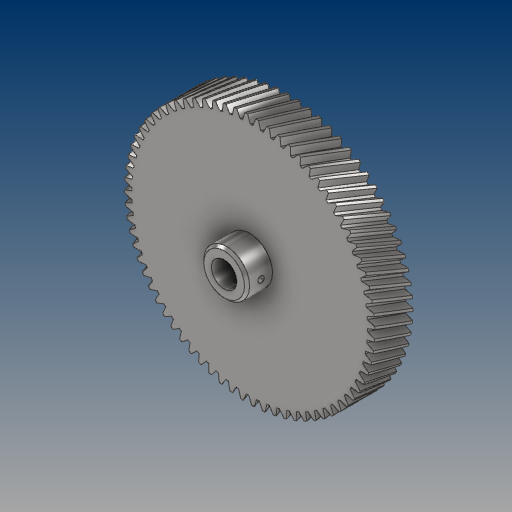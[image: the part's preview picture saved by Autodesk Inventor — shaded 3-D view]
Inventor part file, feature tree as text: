
AUTODESK INVENTOR PART (.ipt)
format: ipt  version: 2021 (Build 250183000, 183)  size: 1,323,008 bytes
history: native  units: mm (DEFAULTED — no unit token found)
features: extrude x4, sketch x4, plane x3, other x3, projected_geometry x2, chamfer x1, pattern_circular x1
ambient origin geometry x8: Origin, YZ Plane, XZ Plane, XY Plane, X Axis, Y Axis, Z Axis, Center Point
bodies: Solid1 (feature_tree)
feature tree (18):
  extrude  "Extrusion1"  Depth=15.0mm TaperAngle=0.0deg
  plane  "Work Plane2"
  plane  "Work Plane8"
  plane  "Work Plane9"
  other  "Spur Gear"
  sketch  "Sketch3"  dims[d16=59.86mm d17=0.0mm d34=0.436332mm]
  extrude  "Extrusion2"  Depth=10.0mm TaperAngle=0.0deg
  extrude  "Extrusion3"  Depth=0.436332mm TaperAngle=0.0deg
  chamfer  "Chamfer1"  [1 undecoded]
  extrude  "Extrusion4"  Depth=15.0mm
  pattern_circular  "Circular Pattern1"  [2 undecoded]
  sketch  "Sketch1"  dims[d0=98.276mm d1=15.0mm d2=0.0mm]
  sketch  "Sketch2"  dims[d3=95.776mm d4=10.0mm d5=0.0mm]
  other  "Srf1"
  projected_geometry  "Projected Loop1"
  sketch  "Sketch4"  dims[d39=0.0mm d41=0.0mm d43=59.86mm d46=59.86mm d47=0.0mm d48=0.0mm d49=10.0mm d50=4.0mm d51=22.0mm d52=0.0mm d53=10.0mm d54=0.0mm d55=1.0mm d56=2.0mm d57=45.0deg d58=2.5mm d59=15.0mm d60=0.0mm d61=20.0mm d62=90.0deg]
  projected_geometry  "Projected Loop2"
  other  "Pitch Diameter"
note: 3 required parameter values undecoded (feature->parameter linkage not recoverable at this tier; creation-order binding heuristic only, values carry confidence <= 0.55)
